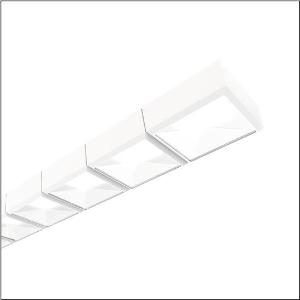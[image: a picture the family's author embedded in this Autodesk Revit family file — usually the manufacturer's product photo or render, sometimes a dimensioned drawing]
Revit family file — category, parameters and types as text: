
# Revit family: scriptus_r__11_5mz312d04wa_0fc2
name_source: partatom
category: Lighting Fixtures
units: mm (PartAtom-declared; Revit-internal decimal feet)

## family parameters
Cut with Voids When Loaded = No
Host = Face
Light Source = No
Part Type = Normal
Room Calculation Point = No
Round Connector Dimension = Use Diameter
Shared = No

## types (1)
- Scriptus® 11 (1 x LED 4000K / CRI = 80 (unbekannt), 1610 lm / 2410 lm, 4000K)
    Apparent Load = 62 VA
    CIE Flux Codes = - - - 0 100 / 82 95 99 100 100
    Color Rendering = 80
    Color Temperature = 4000K
    Default Elevation = 1800 mm
    Description = Scriptus® 11, office luminaire, primary optical cover: lenses, CAT 2 (L<= 3000cd/m²), light emission: direct/indirect distribution, primary light characteristic: symmetric, installation type: suspended mounting, LED, rated luminous flux: 8.020lm, luminous efficacy: 130lm/W, light colour: 840, colour temperature: 4000K, control gear: ECG DALI, with terminal, 5-pole, mains connection: 230V, AC, 50Hz, rated input power: 62W, LED, control gear: ECG DALI, housing, luminaire housing, of aluminium, traffic white (RAL 9016), length: 1.658mm, width: 114mm, height: 57mm, protection rating (complete): IP20, insulation class (complete): insulation class I (protective earthing), certification: CE, ENEC, VDE, protection symbol: F, permissible operating ambient temperature: 0..+35°C, standard: EN 50419, packaging unit: 1 piece
    Height = 57 mm
    Lamp = 1 x LED 4000K / CRI >= 80 (unbekannt)
    Lamp Light Flux = 1610 lm / 2410 lm
    Lamp count = 1
    Length = 1658 mm
    Luminous efficacy = 131 lm/W
    Manufacturer = Siteco
    ModVariant = No
    Model = 5MZ312D04WA
    Mounting Place = Ceiling
    Mounting Type = Pendant
    Number of Poles = 1
    OnlyDefault = Yes
    Power Factor = 1
    Product Name = Scriptus® 11
    Product group = office luminaire | ceiling pendant
    ProductGroupID = 902
    Protection Class = Protection class I
    Protection Degree = IP 20
    RLX_Detail_Level = 1
    RLX_Emergency_Light_Flux = 0 lm
    RLX_Emergency_Type = 0
    RLX_Emergency_Type_DB = No
    RlxData = <blob elided: 31177 chars, md5=9f5458f6>
    Socket = socket
    Standby Power = 0 W
    System Light Flux = 8040 lm
    System Power = 62 W
    Type Comments = Product without accessories
    Type Image = l_1004839.jpg
    URL = http://relux.com
    VarID = ---
    Voltage = 0 V
    Weight = 0.00 kg
    Width = 114 mm

## geometry (parser evidence)
native form markers: Blend x4, Sweep x20
no freeform markers — native parametric forms only
